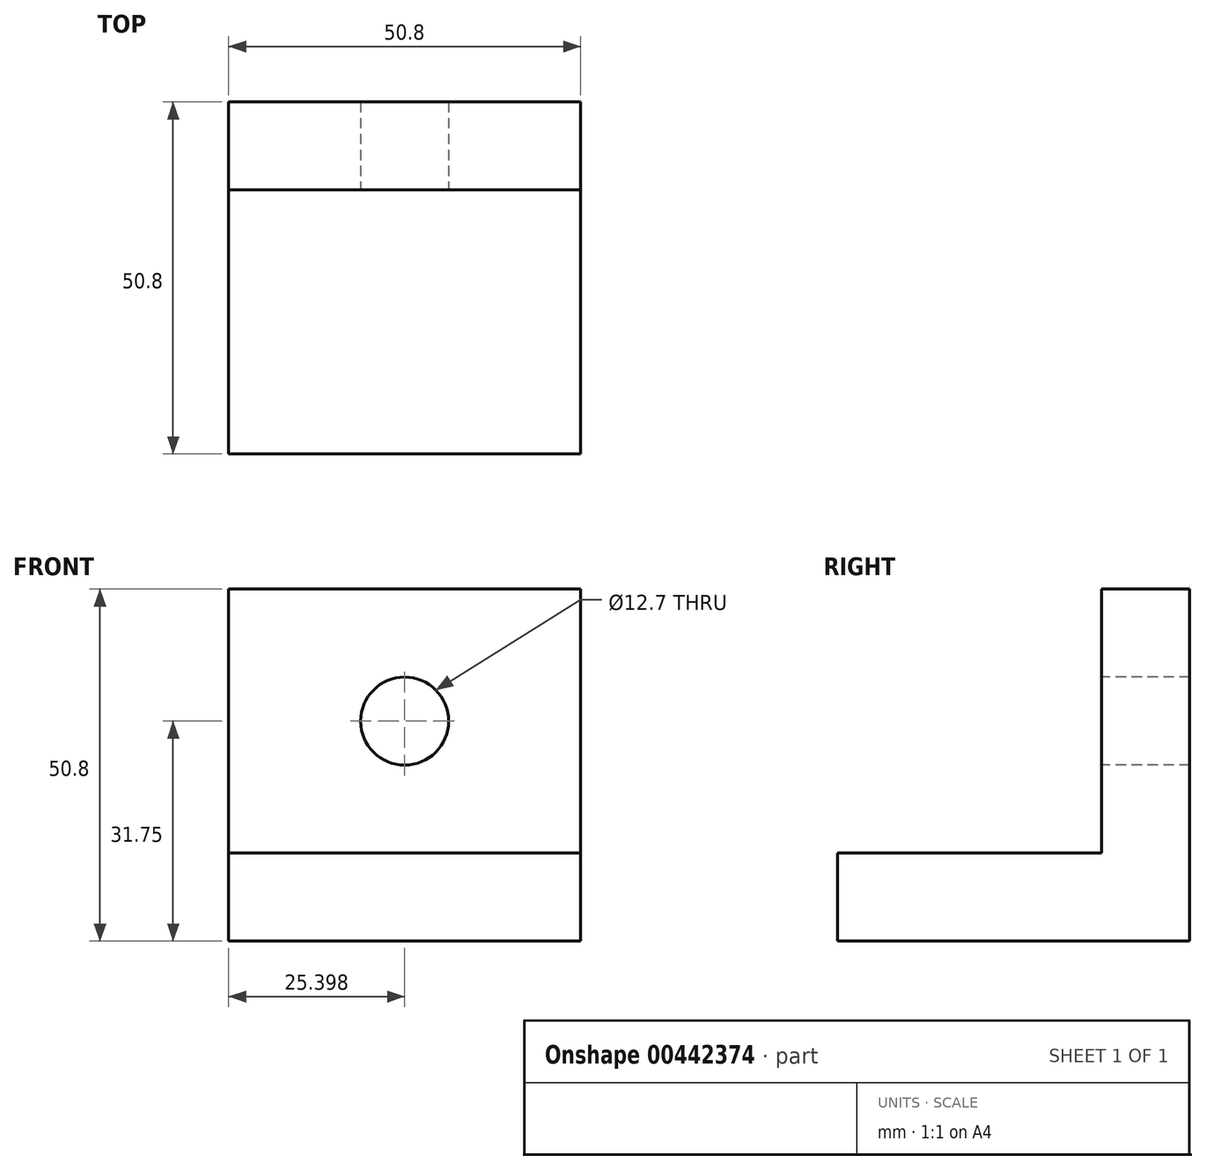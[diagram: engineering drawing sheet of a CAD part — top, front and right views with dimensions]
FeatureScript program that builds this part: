
annotation { "Feature Type Name" : "Feature", "Feature Type Description" : "" }
export const myFeature = defineFeature(function(context is Context, id is Id, definition is map)
    precondition{}
    {
        {
            var Q0;
            Q0=qCreatedBy(makeId("Top.planeOp"),FACE);
            var sketch = newSketch(context, id + "F0", { "sketchPlane" : qUnion([Q0])});
            skLineSegment(sketch, "E0.bottom", {"start": v(-32.51, 37.78) * mm, "end": v(18.29, 37.78) * mm});
            skLineSegment(sketch, "E0.top", {"start": v(-32.51, -13.02) * mm, "end": v(18.29, -13.02) * mm});
            skLineSegment(sketch, "E0.left", {"start": v(-32.51, 37.78) * mm, "end": v(-32.51, -13.02) * mm});
            skLineSegment(sketch, "E0.right", {"start": v(18.29, 37.78) * mm, "end": v(18.29, -13.02) * mm});
            skLineSegment(sketch, "E1", {"start": v(-32.51, 25.08) * mm, "end": v(18.29, 25.08) * mm});
            skPoint(sketch, "E2.endSnap0", {"position": v(-32.51, 12.38) * mm});
            skSolve(sketch);
        }
        {
            var Q0;
            {var subQ0=sQuery(id+"F0.wireOp",EDGE,"E0.bottom");Q0=makeQuery(id+"F0.imprint","IMPRINT",FACE,{"disambiguationData":[TD([[makeQuery(id+"F0.imprint","IMPRINT",EDGE,{"derivedFrom":subQ0}),-1.0]])]});}
            extrude(context, id + "F1", {"entities" : qUnion([Q0]), "depth" : 50.8 * mm});
        }
        {
            var Q0;
            {var subQ0=sQuery(id+"F0.wireOp",EDGE,"E0.top");Q0=makeQuery(id+"F0.imprint","IMPRINT",FACE,{"disambiguationData":[TD([[makeQuery(id+"F0.imprint","IMPRINT",EDGE,{"derivedFrom":subQ0}),1.0]])]});}
            extrude(context, id + "F2", {"entities" : qUnion([Q0]), "operationType" : NewBodyOperationType.ADD, "depth" : 12.7 * mm});
        }
        {
            var Q0;
            Q0=makeQuery(id+"F1.opExtrude","SWEPT_FACE",FACE,{"disambiguationData":[OSD([sQuery(id+"F0.wireOp",EDGE,"E1")])]});
            var sketch = newSketch(context, id + "F3", { "sketchPlane" : qUnion([Q0])});
            skCircle(sketch, "E3", {"center": v(-7.11, 31.75) * mm, "radius": 6.35 * mm});
            skSolve(sketch);
        }
        {
            var Q0;
            Q0=makeQuery(id+"F3.imprint","IMPRINT",FACE,{"disambiguationData":[TD([[makeQuery(id+"F3.imprint","IMPRINT",EDGE,{"derivedFrom":sQuery(id+"F3.wireOp",EDGE,"E3")}),1.0]])]});
            extrude(context, id + "F4", {"entities" : qUnion([Q0]), "operationType" : NewBodyOperationType.REMOVE, "oppositeDirection" : true, "depth" : 12.7 * mm});
        }
    });
